# Revit family: TV201-C-1.9
name_source: partatom
category: Aparatos sanitarios
units: mm (PartAtom-declared; Revit-internal decimal feet)

## family parameters
Compartido = No
Corte con vacíos al cargar = No
Cota de conector redondo = Diámetro de uso
Número OmniClass = 23.45.00.00
Punto de cálculo de habitación = No
Se basa en plano de trabajo = No
Siempre vertical = Sí
Tipo de pieza = Normal
Título OmniClass = Sanitary, Laundry, and Cleaning Equipment

## types (1)
- TV201-C-1.9
    Accesorios = Llave para aireador, Llave allen 2mm, Kit de sujeción, Módulo electrónico
    Chrome = BrassChromed
    Comentarios de tipo = Línea Electrónica
    Conexión AF = No
    Connection = ½" - 14 NPSM
    Descripción = Llave de Lavabo Electrónica de Sensor de Corriente a Pared
    Detection Range = 9.8" (25 cm)
    Elevación por defecto = 0"
    Fabricante = HELVEX
    Feeding Voltage = 6 V
    Max. Working Pressure = 85.3 psi
    Min. Working Pressure = 10.0 psi
    Modelo = TV201-C-1.9
    Operación = Active la salida colocando su mano dentro de la
zona de detección.

## geometry (parser evidence)
native form markers: Sweep x3
no freeform markers — native parametric forms only
